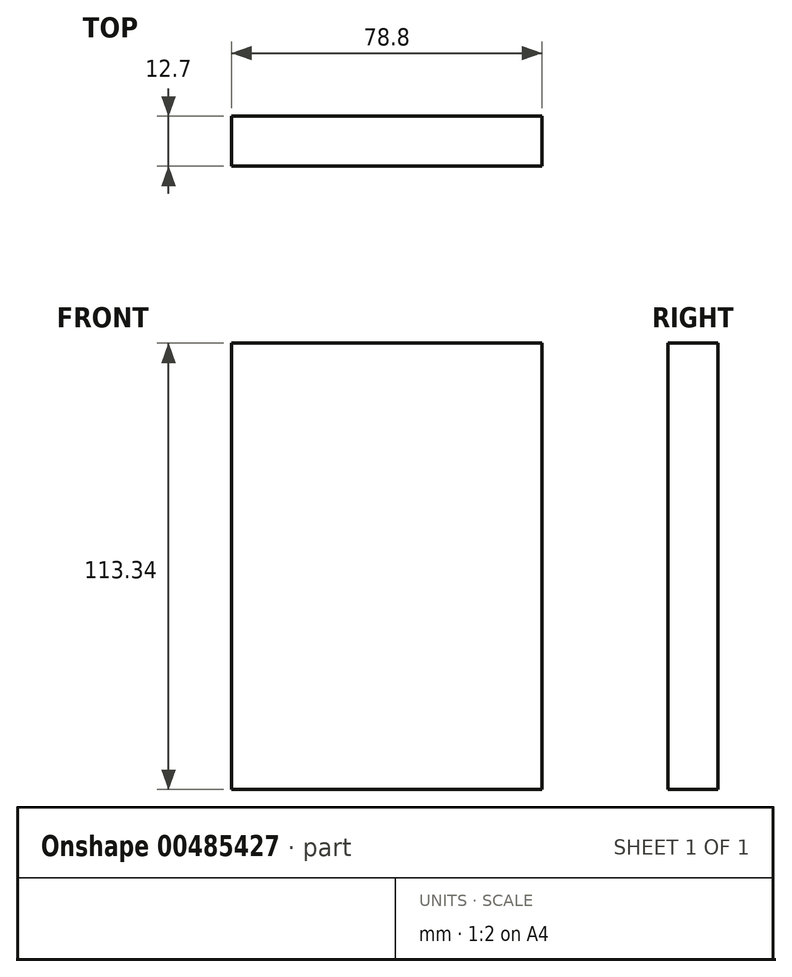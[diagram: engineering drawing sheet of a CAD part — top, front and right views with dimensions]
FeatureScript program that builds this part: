
annotation { "Feature Type Name" : "Feature", "Feature Type Description" : "" }
export const myFeature = defineFeature(function(context is Context, id is Id, definition is map)
    precondition{}
    {
        {
            var Q0;
            Q0=qCreatedBy(makeId("Front.planeOp"),FACE);
            var sketch = newSketch(context, id + "F0", { "sketchPlane" : qUnion([Q0])});
            skLineSegment(sketch, "E0.bottom", {"start": v(39.4, 56.67) * mm, "end": v(-39.4, 56.67) * mm});
            skLineSegment(sketch, "E0.top", {"start": v(39.4, -56.67) * mm, "end": v(-39.4, -56.67) * mm});
            skLineSegment(sketch, "E0.left", {"start": v(39.4, 56.67) * mm, "end": v(39.4, -56.67) * mm});
            skLineSegment(sketch, "E0.right", {"start": v(-39.4, 56.67) * mm, "end": v(-39.4, -56.67) * mm});
            skPoint(sketch, "E0.middle", {"position": v(0, 0) * mm});
            skSolve(sketch);
        }
        {
            var Q0;
            Q0 = qSketchRegion(id + "F0", true);
            var Q1;
            Q1=makeQuery(id+"F0.imprint","IMPRINT",FACE,{"disambiguationData":[TD([[makeQuery(id+"F0.imprint","IMPRINT",EDGE,{"derivedFrom":sQuery(id+"F0.wireOp",EDGE,"E0.bottom")}),1.0]])]});
            extrude(context, id + "F1", {"entities" : qUnion([Q0, Q1]), "depth" : 12.7 * mm});
        }
    });
